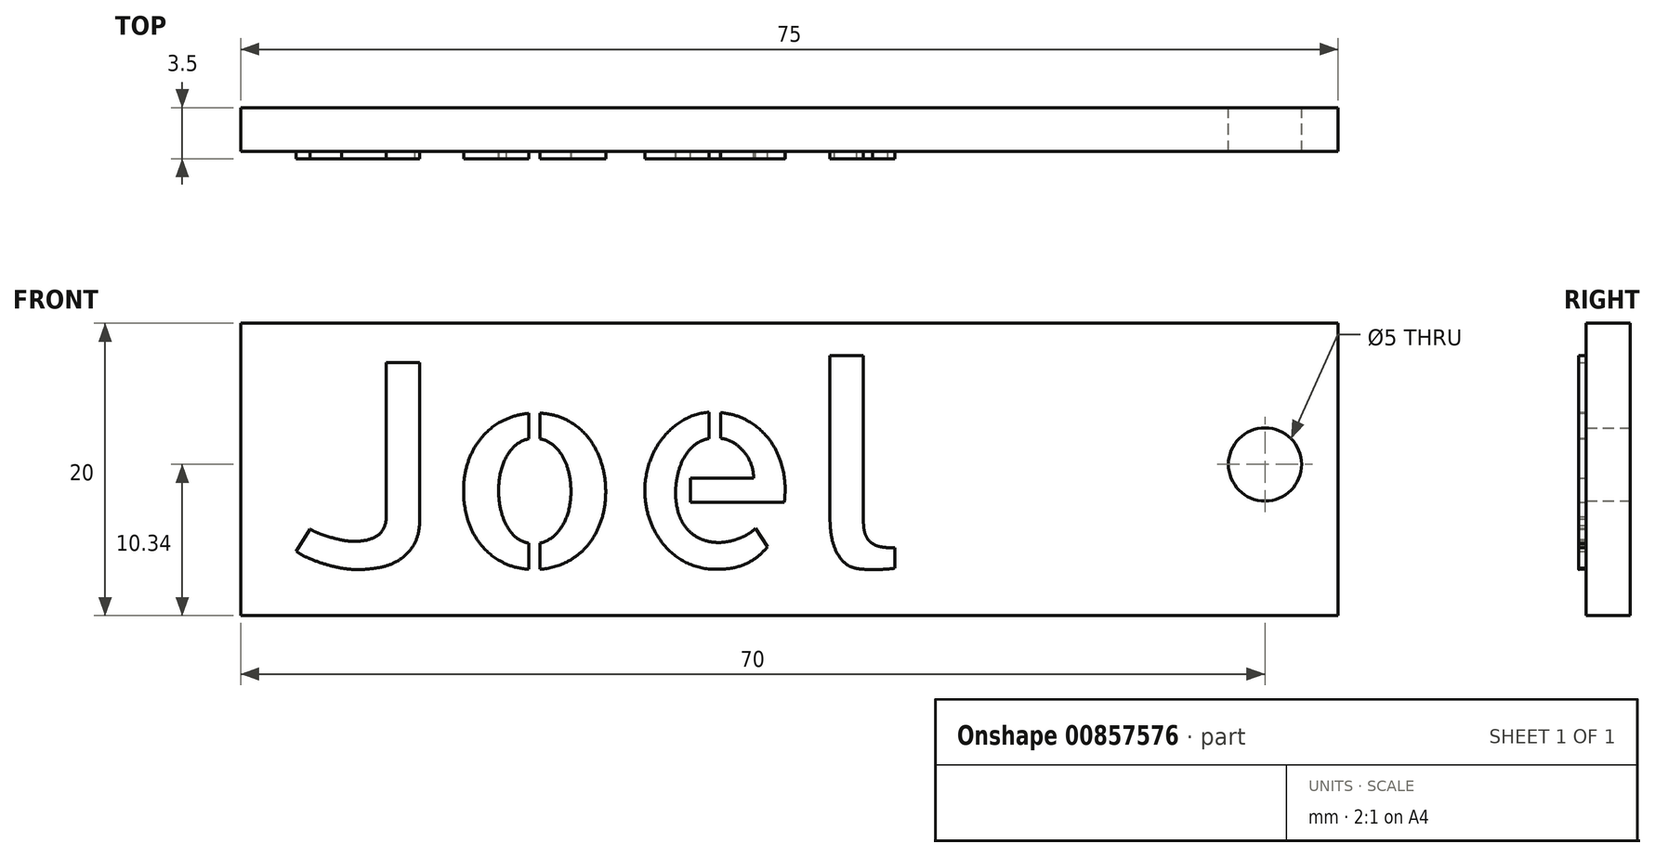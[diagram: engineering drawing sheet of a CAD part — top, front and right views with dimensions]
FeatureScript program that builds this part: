
annotation { "Feature Type Name" : "Feature", "Feature Type Description" : "" }
export const myFeature = defineFeature(function(context is Context, id is Id, definition is map)
    precondition{}
    {
        {
            var Q0;
            Q0=qCreatedBy(makeId("Front.planeOp"),FACE);
            var sketch = newSketch(context, id + "F0", { "sketchPlane" : qUnion([Q0])});
            skLineSegment(sketch, "E0.bottom", {"start": v(0, -20.34) * mm, "end": v(75, -20.34) * mm});
            skLineSegment(sketch, "E0.top", {"start": v(0, -0.34) * mm, "end": v(75, -0.34) * mm});
            skLineSegment(sketch, "E0.left", {"start": v(75, -0.34) * mm, "end": v(75, -20.34) * mm});
            skLineSegment(sketch, "E0.right", {"start": v(0, -0.34) * mm, "end": v(0, -20.34) * mm});
            skCircle(sketch, "E1", {"center": v(70, -10) * mm, "radius": 2.5 * mm});
            skSolve(sketch);
        }
        {
            var Q0;
            Q0=makeQuery(id+"F0.imprint","IMPRINT",FACE,{"disambiguationData":[TD([[makeQuery(id+"F0.imprint","IMPRINT",EDGE,{"derivedFrom":sQuery(id+"F0.wireOp",EDGE,"E0.bottom")}),1.0]])]});
            var sketch = newSketch(context, id + "F1", { "sketchPlane" : qUnion([Q0])});
            skText(sketch, "E2", { "text": "Joel", "fontName": "AllertaStencil-Regular.ttf"});
            const initialGuessF1  = {"E2": [0.0033, -0.0171, 1, 0, 0.0138]};
            skSetInitialGuess(sketch, initialGuessF1);
            skSolve(sketch);
        }
        {
            var Q0;
            Q0 = qSketchRegion(id + "F0", true);
            extrude(context, id + "F2", {"entities" : qUnion([Q0]), "depth" : 3 * mm, "offsetDistance" : 25 * mm});
        }
        {
            var Q0;
            Q0 = qSketchRegion(id + "F1", true);
            extrude(context, id + "F3", {"entities" : qUnion([Q0]), "operationType" : NewBodyOperationType.ADD, "depth" : 3.5 * mm, "offsetDistance" : 25 * mm});
        }
    });
